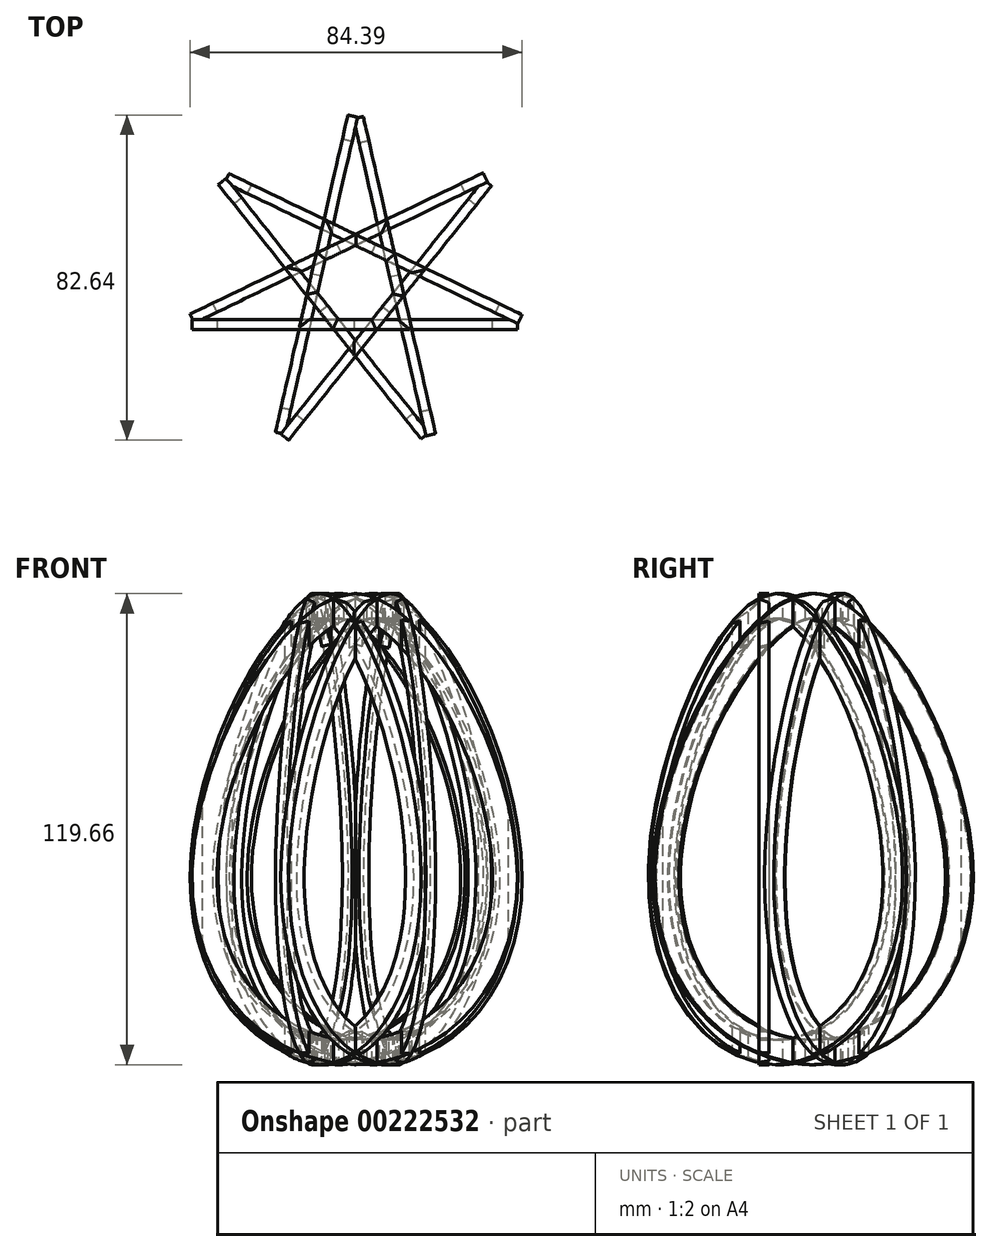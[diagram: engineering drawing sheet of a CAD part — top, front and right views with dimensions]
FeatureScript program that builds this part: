
annotation { "Feature Type Name" : "Feature", "Feature Type Description" : "" }
export const myFeature = defineFeature(function(context is Context, id is Id, definition is map)
    precondition{}
    {
        {
            var Q0;
            Q0=qCreatedBy(makeId("Front.planeOp"),FACE);
            cPlane(context, id + "F0", {"entities" : qUnion([Q0]), "cplaneType" : CPlaneType.OFFSET, "offset" : 8.9 * mm, "width" : 152.4 * mm, "height" : 152.4 * mm});
        }
        {
            var Q0;
            Q0=qCreatedBy(id+"F0.planeOp",FACE);
            var sketch = newSketch(context, id + "F1", { "sketchPlane" : qUnion([Q0])});
            skFitSpline(sketch, "E0", {"points": [v(0, 61.36) * mm, v(-41.33, -10.16) * mm, v(0, -58.3) * mm], "startDerivative": vector(-98.11, 0) * mm, "endDerivative": vector(154.03, -5.63) * mm});
            skLineSegment(sketch, "E1", {"start": v(0, 61.36) * mm, "end": v(0, -58.3) * mm, "construction": true});
            skFitSpline(sketch, "E2.MirrorCS", {"points": [v(0, 61.36) * mm, v(41.33, -10.16) * mm, v(0, -58.3) * mm], "startDerivative": vector(98.11, 0) * mm, "endDerivative": vector(-154.03, -5.63) * mm});
            skFitSpline(sketch, "E3.0", {"points": [v(0, 55.01) * mm, v(0.45, 55.01) * mm, v(1.48, 54.9) * mm, v(3.54, 54.16) * mm, v(6, 52.74) * mm, v(8.72, 50.64) * mm, v(11.57, 47.9) * mm, v(15.45, 43.49) * mm, v(20.24, 36.7) * mm, v(25.5, 27.1) * mm, v(29.9, 16.57) * mm, v(32.6, 7.48) * mm, v(34.06, 0.32) * mm, v(34.64, -4.06) * mm, v(34.9, -7.47) * mm, v(35, -9.97) * mm, v(34.97, -12.4) * mm, v(34.8, -15.57) * mm, v(34.35, -19.4) * mm, v(33.1, -25.2) * mm, v(30.64, -31.8) * mm, v(26.43, -38.6) * mm, v(21.13, -44.13) * mm, v(14.88, -48.32) * mm, v(7.78, -51.07) * mm, v(2.52, -51.86) * mm, v(-0.23, -51.96) * mm]});
            skFitSpline(sketch, "E4.0", {"points": [v(0, 55.01) * mm, v(-0.45, 55.01) * mm, v(-1.48, 54.9) * mm, v(-3.54, 54.16) * mm, v(-6, 52.74) * mm, v(-8.72, 50.64) * mm, v(-11.57, 47.9) * mm, v(-15.45, 43.49) * mm, v(-20.24, 36.7) * mm, v(-25.5, 27.1) * mm, v(-29.9, 16.57) * mm, v(-32.6, 7.48) * mm, v(-34.06, 0.32) * mm, v(-34.64, -4.06) * mm, v(-34.9, -7.47) * mm, v(-35, -9.97) * mm, v(-34.97, -12.4) * mm, v(-34.8, -15.57) * mm, v(-34.35, -19.4) * mm, v(-33.1, -25.2) * mm, v(-30.64, -31.8) * mm, v(-26.43, -38.6) * mm, v(-21.13, -44.13) * mm, v(-14.88, -48.32) * mm, v(-7.78, -51.07) * mm, v(-2.52, -51.86) * mm, v(0.23, -51.96) * mm]});
            skSolve(sketch);
        }
        {
            var Q0;
            Q0=makeQuery(id+"F1.imprint","IMPRINT",FACE,{"disambiguationData":[TD([[makeQuery(id+"F1.imprint","IMPRINT",EDGE,{"derivedFrom":sQuery(id+"F1.wireOp",EDGE,"E0")}),1.0]])]});
            extrude(context, id + "F2", {"entities" : qUnion([Q0]), "depth" : 2.54 * mm});
        }
        {
            var Q0;
            Q0=qCreatedBy(makeId("Front.planeOp"),FACE);
            var sketch = newSketch(context, id + "F3", { "sketchPlane" : qUnion([Q0])});
            skLineSegment(sketch, "E5", {"start": v(0.2, 0) * mm, "end": v(0.2, 79.6) * mm, "construction": true});
            skSolve(sketch);
        }
        {
            var Q0;
            Q0=makeQuery(id+"F2.opExtrude","SWEPT_BODY",BODY,{"disambiguationData":[OSD([sQuery(id+"F1.wireOp",EDGE,"E0"),sQuery(id+"F1.wireOp",EDGE,"E2.MirrorCS"),sQuery(id+"F1.wireOp",EDGE,"E3.0"),sQuery(id+"F1.wireOp",EDGE,"E4.0")])]});
            var Q1;
            Q1=sQuery(id+"F3.wireOp",EDGE,"E5");
            circularPattern(context, id + "F4", {"operationType" : NewBodyOperationType.ADD, "entities" : qUnion([Q0]), "axis" : qUnion([Q1]), "angle" : 360 * degree, "instanceCount" : 7, "equalSpace" : true});
        }
    });
